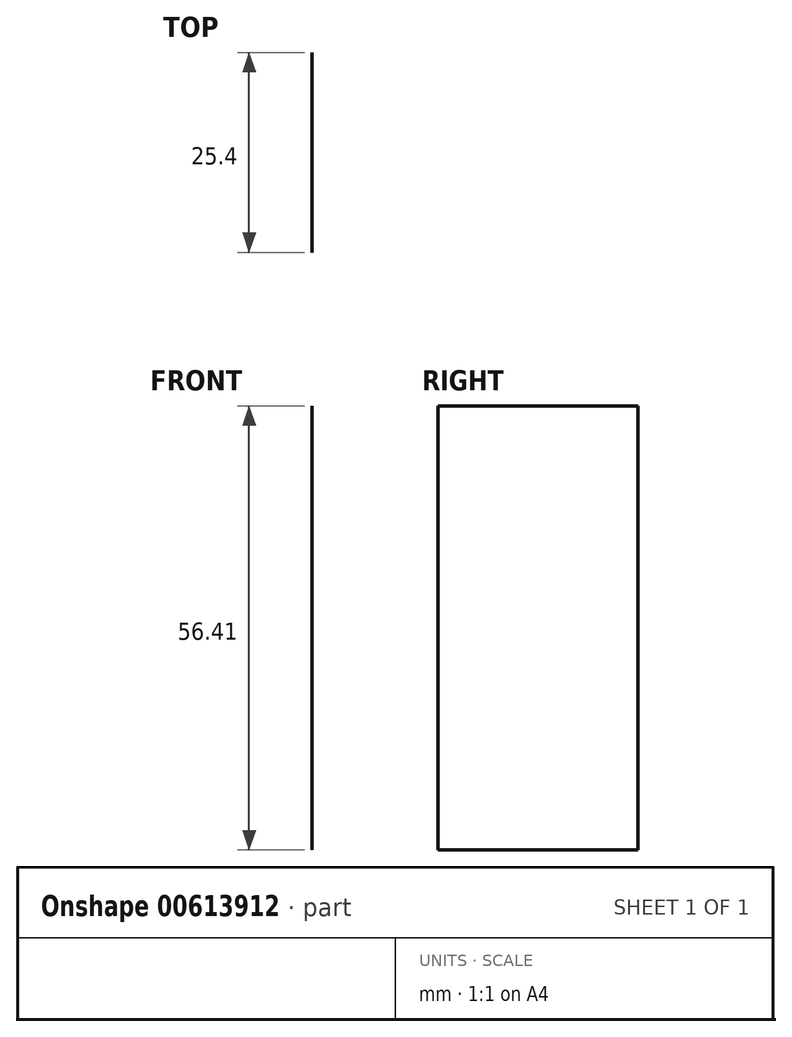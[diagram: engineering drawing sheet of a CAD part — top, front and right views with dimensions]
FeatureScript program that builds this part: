
annotation { "Feature Type Name" : "Feature", "Feature Type Description" : "" }
export const myFeature = defineFeature(function(context is Context, id is Id, definition is map)
    precondition{}
    {
        {
            var Q0;
            Q0=qCreatedBy(makeId("Front.planeOp"),FACE);
            var sketch = newSketch(context, id + "F0", { "sketchPlane" : qUnion([Q0])});
            skLineSegment(sketch, "E0", {"start": v(-66.05, 26.9) * mm, "end": v(-66.05, -29.5) * mm});
            skLineSegment(sketch, "E1", {"start": v(-47.92, -29.5) * mm, "end": v(-47.92, 26.9) * mm});
            skLineSegment(sketch, "E2", {"start": v(-47.92, 26.9) * mm, "end": v(-66.05, 26.9) * mm});
            skLineSegment(sketch, "E3", {"start": v(-47.92, 6.19) * mm, "end": v(12.8, 6.19) * mm});
            skLineSegment(sketch, "E4", {"start": v(0, 0) * mm, "end": v(-72.67, 0) * mm});
            skCircle(sketch, "E5", {"center": v(41.3, 2.45) * mm, "radius": 13.04 * mm});
            skCircle(sketch, "E6", {"center": v(41.3, 2.45) * mm, "radius": 7.68 * mm});
            skLineSegment(sketch, "E7", {"start": v(0, 0) * mm, "end": v(41.3, 0) * mm});
            skPoint(sketch, "E8", {"position": v(-56.84, 0) * mm});
            skPoint(sketch, "E9", {"position": v(-66.05, -1.3) * mm});
            skSolve(sketch);
        }
        {
            var Q0;
            Q0=sQuery(id+"F0.wireOp",EDGE,"E1");
            extrude(context, id + "F1", {"bodyType" : ToolBodyType.SURFACE, "surfaceEntities" : qUnion([Q0]), "depth" : 25.4 * mm, "offsetDistance" : 25.4 * mm});
        }
    });
